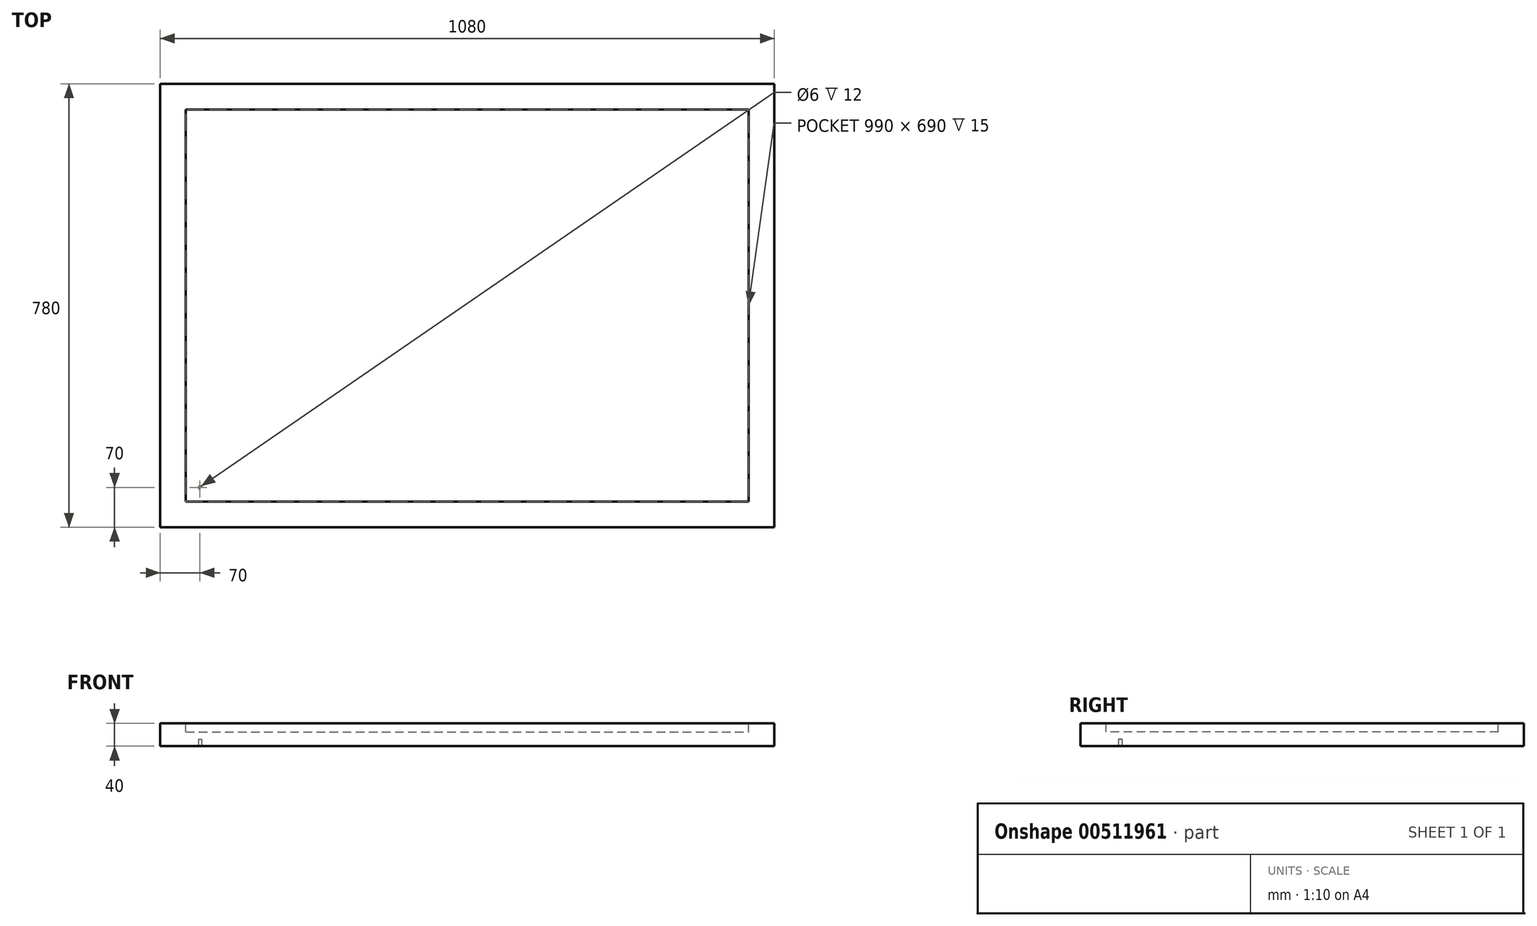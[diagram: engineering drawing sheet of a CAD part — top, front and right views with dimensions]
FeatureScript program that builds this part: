
annotation { "Feature Type Name" : "Feature", "Feature Type Description" : "" }
export const myFeature = defineFeature(function(context is Context, id is Id, definition is map)
    precondition{}
    {
        {
            var Q0;
            Q0=qCreatedBy(makeId("Top.planeOp"),FACE);
            var sketch = newSketch(context, id + "F0", { "sketchPlane" : qUnion([Q0])});
            skLineSegment(sketch, "E0.bottom", {"start": v(0, 0) * mm, "end": v(-1080, 0) * mm});
            skLineSegment(sketch, "E0.top", {"start": v(0, 780) * mm, "end": v(-1080, 780) * mm});
            skLineSegment(sketch, "E0.left", {"start": v(0, 0) * mm, "end": v(0, 780) * mm});
            skLineSegment(sketch, "E0.right", {"start": v(-1080, 0) * mm, "end": v(-1080, 780) * mm});
            skSolve(sketch);
        }
        {
            var Q0;
            Q0=makeQuery(id+"F0.imprint","IMPRINT",FACE,{"disambiguationData":[TD([[makeQuery(id+"F0.imprint","IMPRINT",EDGE,{"derivedFrom":sQuery(id+"F0.wireOp",EDGE,"E0.bottom")}),-1.0]])]});
            extrude(context, id + "F1", {"entities" : qUnion([Q0]), "depth" : 40 * mm, "offsetDistance" : 25 * mm});
        }
        {
            var Q0;
            Q0=makeQuery(id+"F1.opExtrude","CAP_FACE",FACE,{"disambiguationData":[OSD([sQuery(id+"F0.wireOp",EDGE,"E0.bottom"),sQuery(id+"F0.wireOp",EDGE,"E0.top"),sQuery(id+"F0.wireOp",EDGE,"E0.left"),sQuery(id+"F0.wireOp",EDGE,"E0.right")])],"isStart":true});
            var sketch = newSketch(context, id + "F2", { "sketchPlane" : qUnion([Q0])});
            skCircle(sketch, "E1", {"center": v(-1010, -70) * mm, "radius": 3 * mm});
            skSolve(sketch);
        }
        {
            var Q0;
            Q0=makeQuery(id+"F2.imprint","IMPRINT",FACE,{"disambiguationData":[TD([[makeQuery(id+"F2.imprint","IMPRINT",EDGE,{"derivedFrom":sQuery(id+"F2.wireOp",EDGE,"E1")}),1.0]])]});
            var Q1;
            Q1=sQuery(id+"F2.wireOp",EDGE,"E1");
            extrude(context, id + "F3", {"entities" : qUnion([Q0]), "operationType" : NewBodyOperationType.REMOVE, "surfaceEntities" : qUnion([Q1]), "oppositeDirection" : true, "depth" : 12 * mm, "offsetDistance" : 25 * mm});
        }
        {
            var Q0;
            Q0=makeQuery(id+"F1.opExtrude","CAP_FACE",FACE,{"disambiguationData":[OSD([sQuery(id+"F0.wireOp",EDGE,"E0.bottom"),sQuery(id+"F0.wireOp",EDGE,"E0.top"),sQuery(id+"F0.wireOp",EDGE,"E0.left"),sQuery(id+"F0.wireOp",EDGE,"E0.right")])],"isStart":false});
            var sketch = newSketch(context, id + "F4", { "sketchPlane" : qUnion([Q0])});
            skLineSegment(sketch, "E2.bottom", {"start": v(-1035, 735) * mm, "end": v(-45, 735) * mm});
            skLineSegment(sketch, "E2.top", {"start": v(-1035, 45) * mm, "end": v(-45, 45) * mm});
            skLineSegment(sketch, "E2.left", {"start": v(-1035, 735) * mm, "end": v(-1035, 45) * mm});
            skLineSegment(sketch, "E2.right", {"start": v(-45, 735) * mm, "end": v(-45, 45) * mm});
            skSolve(sketch);
        }
        {
            var Q0;
            Q0=makeQuery(id+"F4.imprint","IMPRINT",FACE,{"disambiguationData":[TD([[makeQuery(id+"F4.imprint","IMPRINT",EDGE,{"derivedFrom":sQuery(id+"F4.wireOp",EDGE,"E2.bottom")}),-1.0]])]});
            extrude(context, id + "F5", {"entities" : qUnion([Q0]), "operationType" : NewBodyOperationType.REMOVE, "oppositeDirection" : true, "depth" : 15 * mm, "offsetDistance" : 25 * mm});
        }
    });
